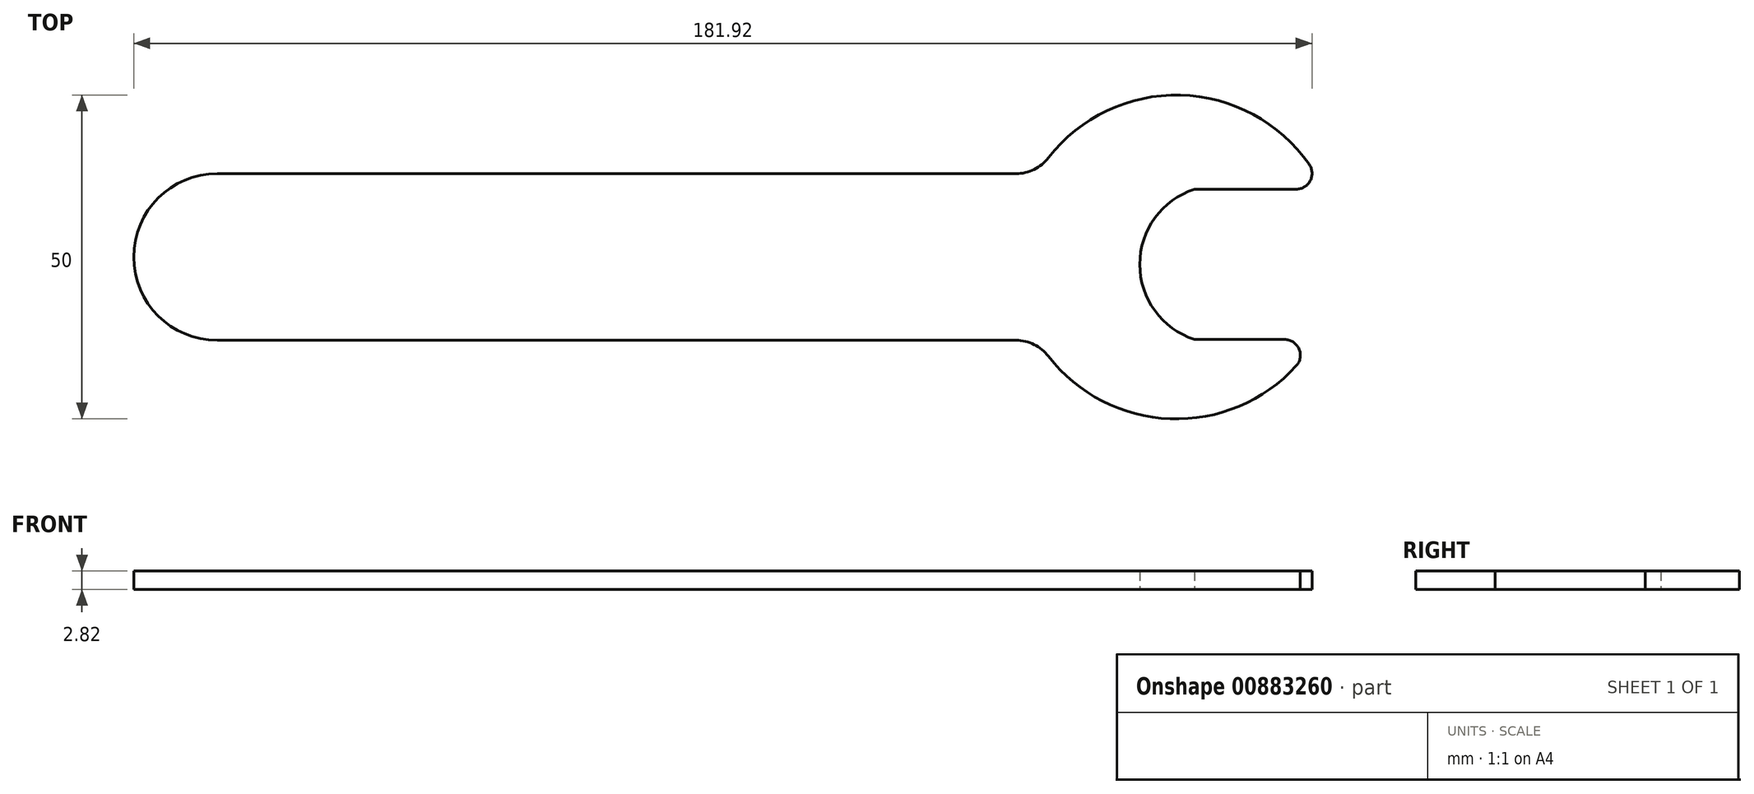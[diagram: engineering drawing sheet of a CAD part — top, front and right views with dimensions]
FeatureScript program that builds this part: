
annotation { "Feature Type Name" : "Feature", "Feature Type Description" : "" }
export const myFeature = defineFeature(function(context is Context, id is Id, definition is map)
    precondition{}
    {
        {
            var Q0;
            Q0=qCreatedBy(makeId("Top.planeOp"),FACE);
            var sketch = newSketch(context, id + "F0", { "sketchPlane" : qUnion([Q0])});
            skLineSegment(sketch, "E0.bottom", {"start": v(-10.93, 25.74) * mm, "end": v(-134.27, 25.74) * mm});
            skLineSegment(sketch, "E0.top", {"start": v(-10.93, 0) * mm, "end": v(-134.27, 0) * mm});
            skArc(sketch, "E1", {"start": v(-5.91, -2.46) * mm, "mid": v(12.87, -12.11) * mm, "end": v(32.35, -3.94) * mm});
            skArc(sketch, "E2", {"start": v(-134.27, 25.74) * mm, "mid": v(-147.14, 12.87) * mm, "end": v(-134.27, 0) * mm});
            skPoint(sketch, "E3.visualSharp", {"position": v(-7.6, 0) * mm});
            skArc(sketch, "E3.filletArc", {"start": v(-5.91, -2.46) * mm, "mid": v(-8.14, -0.65) * mm, "end": v(-10.93, 0) * mm});
            skPoint(sketch, "E4.visualSharp", {"position": v(-7.6, 25.74) * mm});
            skLineSegment(sketch, "E5", {"start": v(16.63, 23.34) * mm, "end": v(32.35, 23.34) * mm});
            skLineSegment(sketch, "E6", {"start": v(16.63, 0.14) * mm, "end": v(30.54, 0.14) * mm});
            skArc(sketch, "E7.trimOffspring", {"start": v(34.34, 27.17) * mm, "mid": v(14.48, 37.86) * mm, "end": v(-5.91, 28.2) * mm});
            skPoint(sketch, "E8.visualSharp", {"position": v(36.54, 23.34) * mm});
            skArc(sketch, "E8.filletArc", {"start": v(32.35, 23.34) * mm, "mid": v(34.5, 24.65) * mm, "end": v(34.34, 27.17) * mm});
            skPoint(sketch, "E9.newPointA", {"position": v(36.54, 0.14) * mm});
            skArc(sketch, "E9.filletArc", {"start": v(32.35, -3.94) * mm, "mid": v(32.77, -1.31) * mm, "end": v(30.54, 0.14) * mm});
            skArc(sketch, "E10.filletArc", {"start": v(-10.93, 25.74) * mm, "mid": v(-8.14, 26.39) * mm, "end": v(-5.91, 28.2) * mm});
            skArc(sketch, "E11", {"start": v(16.63, 23.34) * mm, "mid": v(8.18, 11.74) * mm, "end": v(16.63, 0.14) * mm});
            skSolve(sketch);
        }
        {
            var Q0;
            Q0=makeQuery(id+"F0.imprint","IMPRINT",FACE,{"disambiguationData":[TD([[makeQuery(id+"F0.imprint","IMPRINT",EDGE,{"derivedFrom":sQuery(id+"F0.wireOp",EDGE,"E0.bottom")}),1.0]])]});
            extrude(context, id + "F1", {"entities" : qUnion([Q0]), "depth" : 2.82 * mm, "offsetDistance" : 25.4 * mm});
        }
    });
